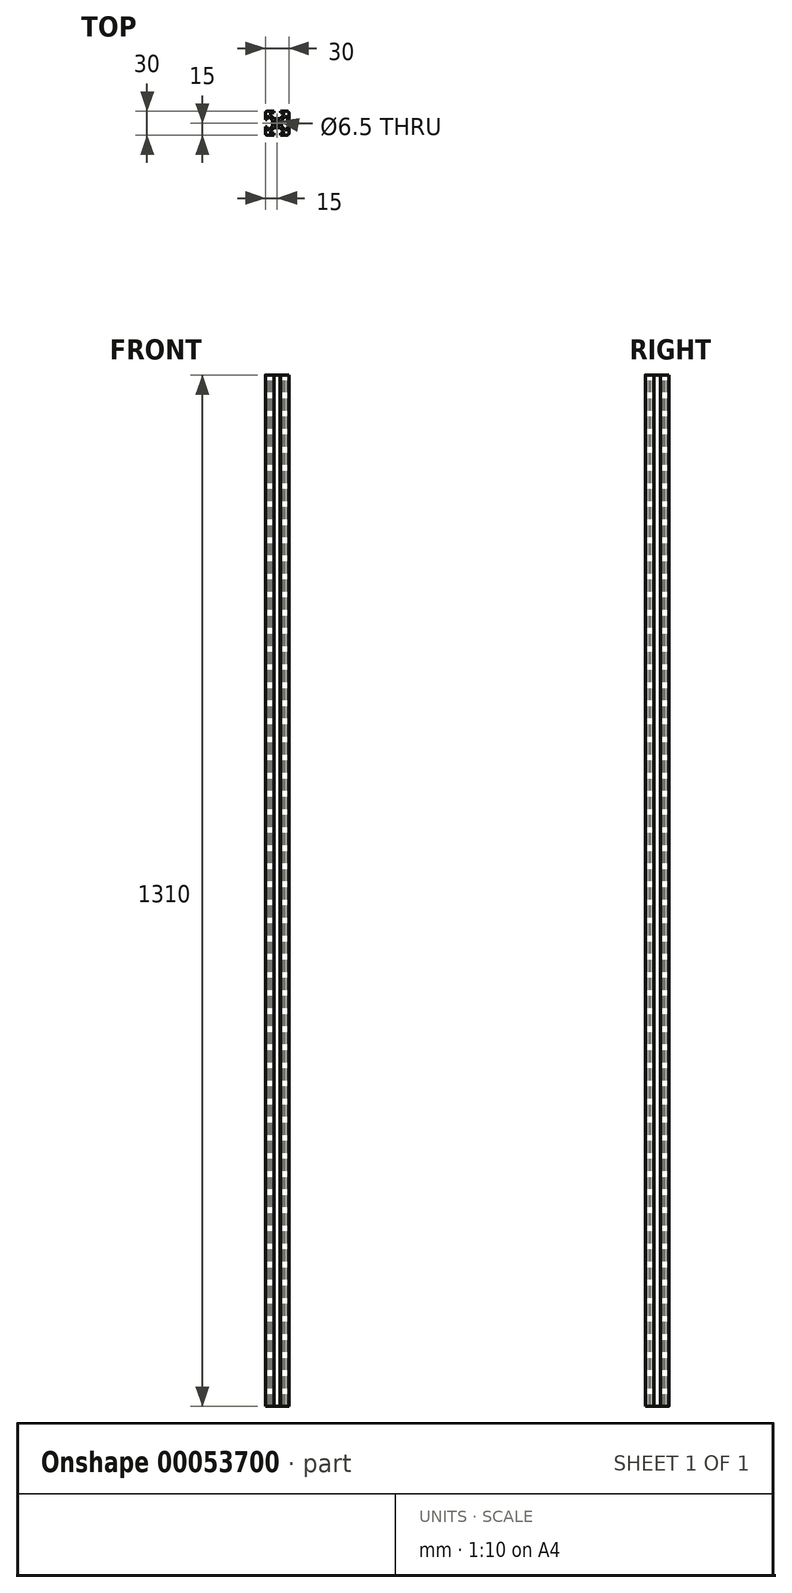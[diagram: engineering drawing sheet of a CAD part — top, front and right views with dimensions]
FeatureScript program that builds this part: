
annotation { "Feature Type Name" : "Feature", "Feature Type Description" : "" }
export const myFeature = defineFeature(function(context is Context, id is Id, definition is map)
    precondition{}
    {
        {
            var Q0;
            Q0=qCreatedBy(makeId("Top.planeOp"),FACE);
            var sketch = newSketch(context, id + "F0", { "sketchPlane" : qUnion([Q0])});
            skLineSegment(sketch, "E0.bottom", {"start": v(-15, 15) * mm, "end": v(15, 15) * mm});
            skLineSegment(sketch, "E0.top", {"start": v(-15, -15) * mm, "end": v(15, -15) * mm});
            skLineSegment(sketch, "E0.left", {"start": v(-15, 15) * mm, "end": v(-15, -15) * mm});
            skLineSegment(sketch, "E0.right", {"start": v(15, 15) * mm, "end": v(15, -15) * mm});
            skSolve(sketch);
        }
        {
            var Q0;
            Q0=qSketchRegion(id+"F0",true);
            extrude(context, id + "F1", {"entities" : qUnion([Q0]), "endBound" : BoundingType.SYMMETRIC, "depth" : 1310 * mm});
        }
        {
            var Q0;
            Q0=makeQuery(id+"F1.opExtrude","SWEPT_EDGE",EDGE,{"disambiguationData":[OSD([sQuery(id+"F0.wireOp",EDGE,"E0.bottom"),sQuery(id+"F0.wireOp",EDGE,"E0.right")])]});
            var Q1;
            Q1=makeQuery(id+"F1.opExtrude","SWEPT_EDGE",EDGE,{"disambiguationData":[OSD([sQuery(id+"F0.wireOp",EDGE,"E0.bottom"),sQuery(id+"F0.wireOp",EDGE,"E0.left")])]});
            var Q2;
            Q2=makeQuery(id+"F1.opExtrude","SWEPT_EDGE",EDGE,{"disambiguationData":[OSD([sQuery(id+"F0.wireOp",EDGE,"E0.top"),sQuery(id+"F0.wireOp",EDGE,"E0.right")])]});
            var Q3;
            Q3=makeQuery(id+"F1.opExtrude","SWEPT_EDGE",EDGE,{"disambiguationData":[OSD([sQuery(id+"F0.wireOp",EDGE,"E0.top"),sQuery(id+"F0.wireOp",EDGE,"E0.left")])]});
            fillet(context, id + "F2", {"entities" : qUnion([Q0, Q1, Q2, Q3]), "radius" : 2 * mm, "tangentPropagation" : true, "allowEdgeOverflow" : false});
        }
        {
            var Q0;
            Q0=makeQuery(id+"F1.opExtrude","CAP_FACE",FACE,{"disambiguationData":[OSD([sQuery(id+"F0.wireOp",EDGE,"E0.bottom"),sQuery(id+"F0.wireOp",EDGE,"E0.top"),sQuery(id+"F0.wireOp",EDGE,"E0.left"),sQuery(id+"F0.wireOp",EDGE,"E0.right")])],"isStart":false});
            var sketch = newSketch(context, id + "F3", { "sketchPlane" : qUnion([Q0])});
            skCircle(sketch, "E1", {"center": v(0, 0) * mm, "radius": 3.25 * mm});
            skSolve(sketch);
        }
        {
            var Q0;
            Q0=qSketchRegion(id+"F3",true);
            extrude(context, id + "F4", {"entities" : qUnion([Q0]), "operationType" : NewBodyOperationType.REMOVE, "endBound" : BoundingType.THROUGH_ALL, "oppositeDirection" : true, "depth" : 25 * mm});
        }
        {
            var Q0;
            Q0=makeQuery(id+"F1.opExtrude","CAP_FACE",FACE,{"disambiguationData":[OSD([sQuery(id+"F0.wireOp",EDGE,"E0.bottom"),sQuery(id+"F0.wireOp",EDGE,"E0.top"),sQuery(id+"F0.wireOp",EDGE,"E0.left"),sQuery(id+"F0.wireOp",EDGE,"E0.right")])],"isStart":false});
            var sketch = newSketch(context, id + "F5", { "sketchPlane" : qUnion([Q0])});
            skLineSegment(sketch, "E2", {"start": v(-4.2, 15) * mm, "end": v(4.2, 15) * mm});
            skLineSegment(sketch, "E3", {"start": v(4.2, 15) * mm, "end": v(4.2, 13) * mm});
            skLineSegment(sketch, "E4", {"start": v(4.2, 13) * mm, "end": v(8.25, 13) * mm});
            skLineSegment(sketch, "E5", {"start": v(8.25, 13) * mm, "end": v(8.25, 10) * mm});
            skLineSegment(sketch, "E6", {"start": v(8.25, 10) * mm, "end": v(3.85, 5.6) * mm});
            skLineSegment(sketch, "E7", {"start": v(3.85, 5.6) * mm, "end": v(-3.85, 5.6) * mm});
            skLineSegment(sketch, "E8", {"start": v(-3.85, 5.6) * mm, "end": v(-8.25, 10) * mm});
            skLineSegment(sketch, "E9", {"start": v(-4.2, 15) * mm, "end": v(-4.2, 13) * mm});
            skLineSegment(sketch, "E10", {"start": v(-4.2, 13) * mm, "end": v(-8.25, 13) * mm});
            skLineSegment(sketch, "E11", {"start": v(-8.25, 13) * mm, "end": v(-8.25, 10) * mm});
            skLineSegment(sketch, "E12.1.0", {"start": v(-15, -4.2) * mm, "end": v(-15, 4.2) * mm});
            skLineSegment(sketch, "E12.1.1", {"start": v(-15, 4.2) * mm, "end": v(-13, 4.2) * mm});
            skLineSegment(sketch, "E12.1.2", {"start": v(-13, 4.2) * mm, "end": v(-13, 8.25) * mm});
            skLineSegment(sketch, "E12.1.3", {"start": v(-13, 8.25) * mm, "end": v(-10, 8.25) * mm});
            skLineSegment(sketch, "E12.1.4", {"start": v(-10, 8.25) * mm, "end": v(-5.6, 3.85) * mm});
            skLineSegment(sketch, "E12.1.5", {"start": v(-5.6, 3.85) * mm, "end": v(-5.6, -3.85) * mm});
            skLineSegment(sketch, "E12.1.6", {"start": v(-5.6, -3.85) * mm, "end": v(-10, -8.25) * mm});
            skLineSegment(sketch, "E12.1.7", {"start": v(-13, -8.25) * mm, "end": v(-10, -8.25) * mm});
            skLineSegment(sketch, "E12.1.8", {"start": v(-13, -4.2) * mm, "end": v(-13, -8.25) * mm});
            skLineSegment(sketch, "E12.1.9", {"start": v(-15, -4.2) * mm, "end": v(-13, -4.2) * mm});
            skLineSegment(sketch, "E12.2.0", {"start": v(4.2, -15) * mm, "end": v(-4.2, -15) * mm});
            skLineSegment(sketch, "E12.2.1", {"start": v(-4.2, -15) * mm, "end": v(-4.2, -13) * mm});
            skLineSegment(sketch, "E12.2.2", {"start": v(-4.2, -13) * mm, "end": v(-8.25, -13) * mm});
            skLineSegment(sketch, "E12.2.3", {"start": v(-8.25, -13) * mm, "end": v(-8.25, -10) * mm});
            skLineSegment(sketch, "E12.2.4", {"start": v(-8.25, -10) * mm, "end": v(-3.85, -5.6) * mm});
            skLineSegment(sketch, "E12.2.5", {"start": v(-3.85, -5.6) * mm, "end": v(3.85, -5.6) * mm});
            skLineSegment(sketch, "E12.2.6", {"start": v(3.85, -5.6) * mm, "end": v(8.25, -10) * mm});
            skLineSegment(sketch, "E12.2.7", {"start": v(8.25, -13) * mm, "end": v(8.25, -10) * mm});
            skLineSegment(sketch, "E12.2.8", {"start": v(4.2, -13) * mm, "end": v(8.25, -13) * mm});
            skLineSegment(sketch, "E12.2.9", {"start": v(4.2, -15) * mm, "end": v(4.2, -13) * mm});
            skLineSegment(sketch, "E12.3.0", {"start": v(15, 4.2) * mm, "end": v(15, -4.2) * mm});
            skLineSegment(sketch, "E12.3.1", {"start": v(15, -4.2) * mm, "end": v(13, -4.2) * mm});
            skLineSegment(sketch, "E12.3.2", {"start": v(13, -4.2) * mm, "end": v(13, -8.25) * mm});
            skLineSegment(sketch, "E12.3.3", {"start": v(13, -8.25) * mm, "end": v(10, -8.25) * mm});
            skLineSegment(sketch, "E12.3.4", {"start": v(10, -8.25) * mm, "end": v(5.6, -3.85) * mm});
            skLineSegment(sketch, "E12.3.5", {"start": v(5.6, -3.85) * mm, "end": v(5.6, 3.85) * mm});
            skLineSegment(sketch, "E12.3.6", {"start": v(5.6, 3.85) * mm, "end": v(10, 8.25) * mm});
            skLineSegment(sketch, "E12.3.7", {"start": v(13, 8.25) * mm, "end": v(10, 8.25) * mm});
            skLineSegment(sketch, "E12.3.8", {"start": v(13, 4.2) * mm, "end": v(13, 8.25) * mm});
            skLineSegment(sketch, "E12.3.9", {"start": v(15, 4.2) * mm, "end": v(13, 4.2) * mm});
            skPoint(sketch, "E12.center", {"position": v(0, 0) * mm});
            skSolve(sketch);
        }
        {
            var Q0;
            Q0=qSketchRegion(id+"F5",true);
            extrude(context, id + "F6", {"entities" : qUnion([Q0]), "operationType" : NewBodyOperationType.REMOVE, "endBound" : BoundingType.THROUGH_ALL, "oppositeDirection" : true, "depth" : 25 * mm});
        }
    });
